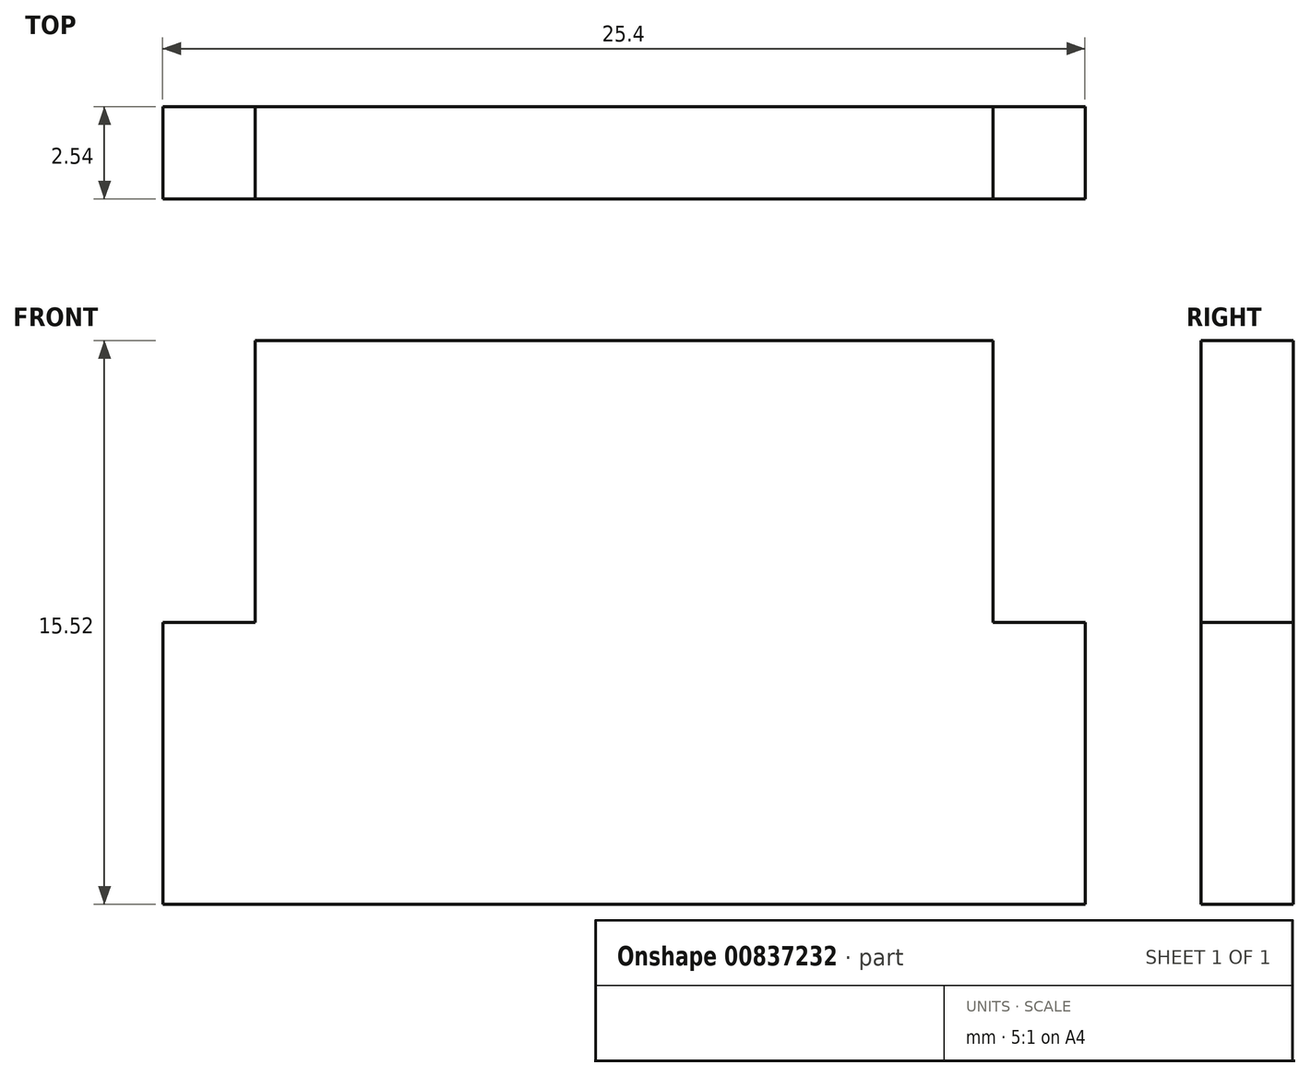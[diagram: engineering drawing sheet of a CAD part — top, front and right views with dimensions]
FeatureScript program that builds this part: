
annotation { "Feature Type Name" : "Feature", "Feature Type Description" : "" }
export const myFeature = defineFeature(function(context is Context, id is Id, definition is map)
    precondition{}
    {
        {
            var Q0;
            Q0=qCreatedBy(makeId("Front.planeOp"),FACE);
            var sketch = newSketch(context, id + "F0", { "sketchPlane" : qUnion([Q0])});
            skLineSegment(sketch, "E0", {"start": v(-74.7, 0) * mm, "end": v(-49.3, 0) * mm});
            skLineSegment(sketch, "E1", {"start": v(-49.3, 0) * mm, "end": v(-49.3, 7.76) * mm});
            skLineSegment(sketch, "E2", {"start": v(-51.84, 15.52) * mm, "end": v(-72.16, 15.52) * mm});
            skLineSegment(sketch, "E3", {"start": v(-74.7, 7.76) * mm, "end": v(-74.7, 0) * mm});
            skLineSegment(sketch, "E4", {"start": v(-74.7, 0) * mm, "end": v(-74.7, 7.76) * mm});
            skLineSegment(sketch, "E5", {"start": v(-74.7, 7.76) * mm, "end": v(-49.3, 7.76) * mm});
            skLineSegment(sketch, "E6", {"start": v(-74.7, 0) * mm, "end": v(-74.7, 3.88) * mm});
            skLineSegment(sketch, "E7", {"start": v(-74.7, 3.88) * mm, "end": v(-49.3, 3.88) * mm});
            skLineSegment(sketch, "E8", {"start": v(-74.7, 0) * mm, "end": v(-62, 0) * mm});
            skLineSegment(sketch, "E9", {"start": v(-62, 7.76) * mm, "end": v(-72.16, 7.76) * mm});
            skLineSegment(sketch, "E10", {"start": v(-62, 7.76) * mm, "end": v(-51.84, 7.76) * mm});
            skLineSegment(sketch, "E11", {"start": v(-72.16, 7.76) * mm, "end": v(-72.16, 10.34) * mm});
            skLineSegment(sketch, "E12", {"start": v(-72.16, 10.34) * mm, "end": v(-51.84, 10.34) * mm});
            skLineSegment(sketch, "E13", {"start": v(-51.84, 10.34) * mm, "end": v(-51.84, 7.76) * mm});
            skLineSegment(sketch, "E14", {"start": v(-72.16, 10.34) * mm, "end": v(-72.16, 12.9) * mm});
            skLineSegment(sketch, "E15", {"start": v(-72.16, 12.9) * mm, "end": v(-51.84, 12.9) * mm});
            skLineSegment(sketch, "E16", {"start": v(-51.84, 12.9) * mm, "end": v(-51.84, 10.34) * mm});
            skLineSegment(sketch, "E17", {"start": v(-72.16, 12.9) * mm, "end": v(-72.16, 15.52) * mm});
            skLineSegment(sketch, "E18", {"start": v(-51.84, 12.9) * mm, "end": v(-51.84, 15.52) * mm});
            skSolve(sketch);
        }
        {
            var Q0;
            Q0 = qSketchRegion(id + "F0", true);
            extrude(context, id + "F1", {"entities" : qUnion([Q0]), "oppositeDirection" : true, "depth" : 2.54 * mm, "offsetDistance" : 25.4 * mm});
        }
    });
